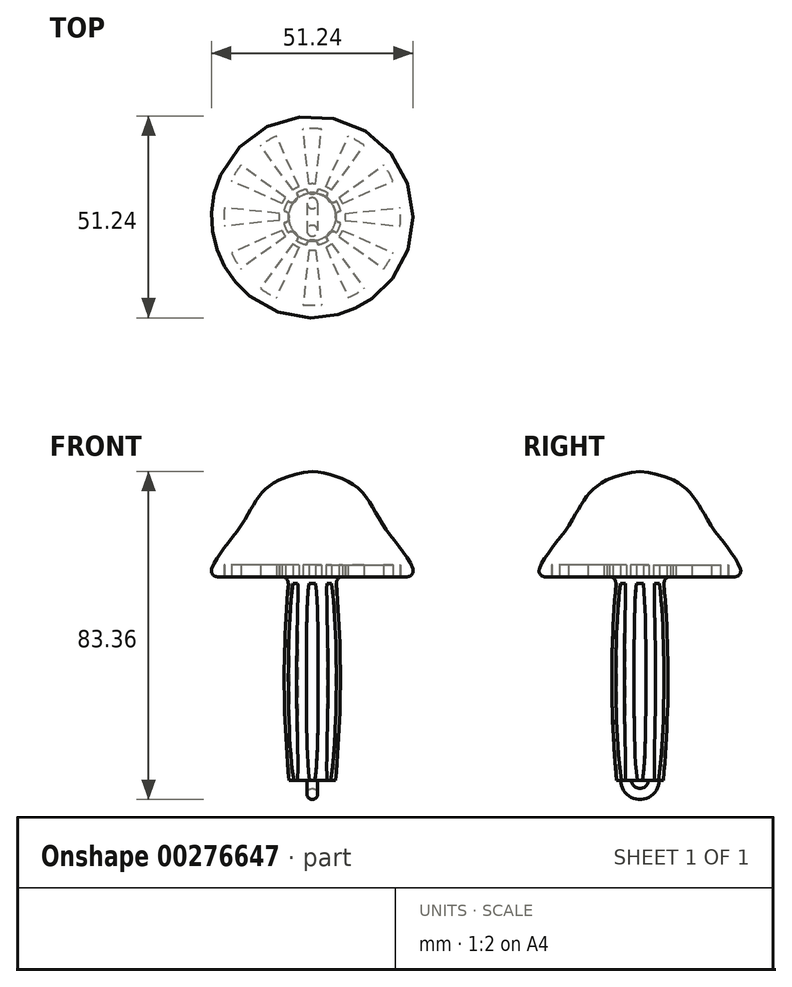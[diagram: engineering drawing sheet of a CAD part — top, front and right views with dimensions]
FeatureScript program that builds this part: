
annotation { "Feature Type Name" : "Feature", "Feature Type Description" : "" }
export const myFeature = defineFeature(function(context is Context, id is Id, definition is map)
    precondition{}
    {
        {
            var Q0;
            Q0=qCreatedBy(makeId("Front.planeOp"),FACE);
            var sketch = newSketch(context, id + "F0", { "sketchPlane" : qUnion([Q0])});
            skLineSegment(sketch, "E0", {"start": v(0, 0) * mm, "end": v(6, 0) * mm});
            skLineSegment(sketch, "E1", {"start": v(0, 69.05) * mm, "end": v(0, 0) * mm});
            skArc(sketch, "E2", {"start": v(6, 0) * mm, "mid": v(7.3, 25.84) * mm, "end": v(6, 51.68) * mm});
            skLineSegment(sketch, "E3", {"start": v(6, 51.68) * mm, "end": v(26, 51.68) * mm});
            skLineSegment(sketch, "E4", {"start": v(0, 69.05) * mm, "end": v(0, 78.48) * mm});
            skFitSpline(sketch, "E5", {"points": [v(26, 51.68) * mm, v(18.55, 63.96) * mm, v(11.44, 74.34) * mm, v(0, 78.48) * mm], "startDerivative": vector(-3.83, 37.04) * mm, "endDerivative": vector(-33.85, 3.07) * mm});
            skSolve(sketch);
        }
        {
            var Q0;
            Q0=makeQuery(id+"F0.imprint","IMPRINT",FACE,{"disambiguationData":[TD([[makeQuery(id+"F0.imprint","IMPRINT",EDGE,{"derivedFrom":sQuery(id+"F0.wireOp",EDGE,"E0")}),1.0]])]});
            var Q1;
            Q1=sQuery(id+"F0.wireOp",EDGE,"E1");
            revolve(context, id + "F1", {"entities" : qUnion([Q0]), "axis" : qUnion([Q1]), "revolveType" : RevolveType.FULL});
        }
        {
            var Q0;
            Q0=makeQuery(id+"F1.opRevolve","SWEPT_FACE",FACE,{"disambiguationData":[OSD([sQuery(id+"F0.wireOp",EDGE,"E3")])]});
            var Q1;
            Q1=makeQuery(id+"F1.opRevolve","SWEPT_FACE",FACE,{"disambiguationData":[OSD([sQuery(id+"F0.wireOp",EDGE,"Vve0fadS-4mgB-wVBS-b9aS-wJGoKtQ9clZr")])]});
            fillet(context, id + "F2", {"entities" : qUnion([Q0, Q1]), "radius" : 1.5 * mm, "tangentPropagation" : true, "allowEdgeOverflow" : false});
        }
        {
            var Q0;
            Q0=qCreatedBy(makeId("Top.planeOp"),FACE);
            var sketch = newSketch(context, id + "F3", { "sketchPlane" : qUnion([Q0])});
            skLineSegment(sketch, "E6", {"start": v(0, 0) * mm, "end": v(14.37, 0) * mm, "construction": true});
            skCircle(sketch, "E7", {"center": v(0, -3.5) * mm, "radius": 1.38 * mm});
            skSolve(sketch);
        }
        {
            var Q0;
            Q0 = qSketchRegion(id + "F3", true);
            var Q1;
            Q1=sQuery(id+"F3.wireOp",EDGE,"E6");
            revolve(context, id + "F4", {"operationType" : NewBodyOperationType.ADD, "entities" : qUnion([Q0]), "axis" : qUnion([Q1]), "revolveType" : RevolveType.ONE_DIRECTION, "angle" : 180 * degree});
        }
        {
            var Q0;
            Q0=makeQuery(id+"F1.opRevolve","SWEPT_FACE",FACE,{"disambiguationData":[OSD([sQuery(id+"F0.wireOp",EDGE,"E0")])]});
            var sketch = newSketch(context, id + "F5", { "sketchPlane" : qUnion([Q0])});
            skLineSegment(sketch, "E8", {"start": v(0, 0) * mm, "end": v(0, 7.31) * mm});
            skCircle(sketch, "E9", {"center": v(0, 7.31) * mm, "radius": 1.5 * mm});
            skCircle(sketch, "E10.1.0", {"center": v(-5.17, 5.17) * mm, "radius": 1.5 * mm});
            skCircle(sketch, "E10.2.0", {"center": v(-7.31, 0) * mm, "radius": 1.5 * mm});
            skCircle(sketch, "E10.3.0", {"center": v(-5.17, -5.17) * mm, "radius": 1.5 * mm});
            skCircle(sketch, "E10.4.0", {"center": v(0, -7.31) * mm, "radius": 1.5 * mm});
            skCircle(sketch, "E10.5.0", {"center": v(5.17, -5.17) * mm, "radius": 1.5 * mm});
            skCircle(sketch, "E10.6.0", {"center": v(7.31, 0) * mm, "radius": 1.5 * mm});
            skCircle(sketch, "E10.7.0", {"center": v(5.17, 5.17) * mm, "radius": 1.5 * mm});
            skPoint(sketch, "E10.center", {"position": v(0, 0) * mm});
            skSolve(sketch);
        }
        {
            var Q0;
            Q0 = qSketchRegion(id + "F5", true);
            extrude(context, id + "F6", {"entities" : qUnion([Q0]), "operationType" : NewBodyOperationType.REMOVE, "oppositeDirection" : true, "depth" : 50 * mm});
        }
        {
            var Q0;
            Q0=makeQuery(id+"F1.opRevolve","SWEPT_FACE",FACE,{"disambiguationData":[OSD([sQuery(id+"F0.wireOp",EDGE,"E3")])]});
            var sketch = newSketch(context, id + "F7", { "sketchPlane" : qUnion([Q0])});
            skLineSegment(sketch, "E11", {"start": v(0.88, 8.37) * mm, "end": v(2.35, 22.32) * mm});
            skLineSegment(sketch, "E12", {"start": v(-0.88, 8.37) * mm, "end": v(-2.35, 22.32) * mm});
            skArc(sketch, "E13", {"start": v(0.88, 8.37) * mm, "mid": v(0, 8.42) * mm, "end": v(-0.88, 8.37) * mm});
            skArc(sketch, "E14", {"start": v(2.35, 22.32) * mm, "mid": v(0, 22.44) * mm, "end": v(-2.35, 22.32) * mm});
            skPoint(sketch, "E15.trimOffspring.end.orphan", {"position": v(0, 28.12) * mm});
            skPoint(sketch, "E16.orphan", {"position": v(2.96, 28.12) * mm});
            skArc(sketch, "E17.1.0", {"start": v(-9.13, 20.5) * mm, "mid": v(-11.22, 19.43) * mm, "end": v(-13.19, 18.15) * mm});
            skLineSegment(sketch, "E17.1.1", {"start": v(-3.42, 7.7) * mm, "end": v(-9.13, 20.5) * mm});
            skLineSegment(sketch, "E17.1.2", {"start": v(-4.95, 6.81) * mm, "end": v(-13.19, 18.15) * mm});
            skArc(sketch, "E17.1.3", {"start": v(-3.42, 7.7) * mm, "mid": v(-4.2, 7.3) * mm, "end": v(-4.95, 6.81) * mm});
            skArc(sketch, "E17.2.0", {"start": v(-18.15, 13.19) * mm, "mid": v(-19.43, 11.22) * mm, "end": v(-20.5, 9.13) * mm});
            skLineSegment(sketch, "E17.2.1", {"start": v(-6.81, 4.95) * mm, "end": v(-18.15, 13.19) * mm});
            skLineSegment(sketch, "E17.2.2", {"start": v(-7.7, 3.42) * mm, "end": v(-20.5, 9.13) * mm});
            skArc(sketch, "E17.2.3", {"start": v(-6.81, 4.95) * mm, "mid": v(-7.3, 4.2) * mm, "end": v(-7.7, 3.42) * mm});
            skArc(sketch, "E17.3.0", {"start": v(-22.32, 2.35) * mm, "mid": v(-22.44, 0) * mm, "end": v(-22.32, -2.35) * mm});
            skLineSegment(sketch, "E17.3.1", {"start": v(-8.37, 0.88) * mm, "end": v(-22.32, 2.35) * mm});
            skLineSegment(sketch, "E17.3.2", {"start": v(-8.37, -0.88) * mm, "end": v(-22.32, -2.35) * mm});
            skArc(sketch, "E17.3.3", {"start": v(-8.37, 0.88) * mm, "mid": v(-8.42, 0) * mm, "end": v(-8.37, -0.88) * mm});
            skArc(sketch, "E17.4.0", {"start": v(-20.5, -9.13) * mm, "mid": v(-19.43, -11.22) * mm, "end": v(-18.15, -13.19) * mm});
            skLineSegment(sketch, "E17.4.1", {"start": v(-7.7, -3.42) * mm, "end": v(-20.5, -9.13) * mm});
            skLineSegment(sketch, "E17.4.2", {"start": v(-6.81, -4.95) * mm, "end": v(-18.15, -13.19) * mm});
            skArc(sketch, "E17.4.3", {"start": v(-7.7, -3.42) * mm, "mid": v(-7.3, -4.2) * mm, "end": v(-6.81, -4.95) * mm});
            skArc(sketch, "E17.5.0", {"start": v(-13.19, -18.15) * mm, "mid": v(-11.22, -19.43) * mm, "end": v(-9.13, -20.5) * mm});
            skLineSegment(sketch, "E17.5.1", {"start": v(-4.95, -6.81) * mm, "end": v(-13.19, -18.15) * mm});
            skLineSegment(sketch, "E17.5.2", {"start": v(-3.42, -7.7) * mm, "end": v(-9.13, -20.5) * mm});
            skArc(sketch, "E17.5.3", {"start": v(-4.95, -6.81) * mm, "mid": v(-4.2, -7.3) * mm, "end": v(-3.42, -7.7) * mm});
            skArc(sketch, "E17.6.0", {"start": v(-2.35, -22.32) * mm, "mid": v(0, -22.44) * mm, "end": v(2.35, -22.32) * mm});
            skLineSegment(sketch, "E17.6.1", {"start": v(-0.88, -8.37) * mm, "end": v(-2.35, -22.32) * mm});
            skLineSegment(sketch, "E17.6.2", {"start": v(0.88, -8.37) * mm, "end": v(2.35, -22.32) * mm});
            skArc(sketch, "E17.6.3", {"start": v(-0.88, -8.37) * mm, "mid": v(0, -8.42) * mm, "end": v(0.88, -8.37) * mm});
            skArc(sketch, "E17.7.0", {"start": v(9.13, -20.5) * mm, "mid": v(11.22, -19.43) * mm, "end": v(13.19, -18.15) * mm});
            skLineSegment(sketch, "E17.7.1", {"start": v(3.42, -7.7) * mm, "end": v(9.13, -20.5) * mm});
            skLineSegment(sketch, "E17.7.2", {"start": v(4.95, -6.81) * mm, "end": v(13.19, -18.15) * mm});
            skArc(sketch, "E17.7.3", {"start": v(3.42, -7.7) * mm, "mid": v(4.2, -7.3) * mm, "end": v(4.95, -6.81) * mm});
            skArc(sketch, "E17.8.0", {"start": v(18.15, -13.19) * mm, "mid": v(19.43, -11.22) * mm, "end": v(20.5, -9.13) * mm});
            skLineSegment(sketch, "E17.8.1", {"start": v(6.81, -4.95) * mm, "end": v(18.15, -13.19) * mm});
            skLineSegment(sketch, "E17.8.2", {"start": v(7.7, -3.42) * mm, "end": v(20.5, -9.13) * mm});
            skArc(sketch, "E17.8.3", {"start": v(6.81, -4.95) * mm, "mid": v(7.3, -4.2) * mm, "end": v(7.7, -3.42) * mm});
            skArc(sketch, "E17.9.0", {"start": v(22.32, -2.35) * mm, "mid": v(22.44, 0) * mm, "end": v(22.32, 2.35) * mm});
            skLineSegment(sketch, "E17.9.1", {"start": v(8.37, -0.88) * mm, "end": v(22.32, -2.35) * mm});
            skLineSegment(sketch, "E17.9.2", {"start": v(8.37, 0.88) * mm, "end": v(22.32, 2.35) * mm});
            skArc(sketch, "E17.9.3", {"start": v(8.37, -0.88) * mm, "mid": v(8.42, 0) * mm, "end": v(8.37, 0.88) * mm});
            skArc(sketch, "E17.10.0", {"start": v(20.5, 9.13) * mm, "mid": v(19.43, 11.22) * mm, "end": v(18.15, 13.19) * mm});
            skLineSegment(sketch, "E17.10.1", {"start": v(7.7, 3.42) * mm, "end": v(20.5, 9.13) * mm});
            skLineSegment(sketch, "E17.10.2", {"start": v(6.81, 4.95) * mm, "end": v(18.15, 13.19) * mm});
            skArc(sketch, "E17.10.3", {"start": v(7.7, 3.42) * mm, "mid": v(7.3, 4.2) * mm, "end": v(6.81, 4.95) * mm});
            skArc(sketch, "E17.11.0", {"start": v(13.19, 18.15) * mm, "mid": v(11.22, 19.43) * mm, "end": v(9.13, 20.5) * mm});
            skLineSegment(sketch, "E17.11.1", {"start": v(4.95, 6.81) * mm, "end": v(13.19, 18.15) * mm});
            skLineSegment(sketch, "E17.11.2", {"start": v(3.42, 7.7) * mm, "end": v(9.13, 20.5) * mm});
            skArc(sketch, "E17.11.3", {"start": v(4.95, 6.81) * mm, "mid": v(4.2, 7.3) * mm, "end": v(3.42, 7.7) * mm});
            skSolve(sketch);
        }
        {
            var Q0;
            Q0 = qSketchRegion(id + "F7", true);
            extrude(context, id + "F8", {"entities" : qUnion([Q0]), "operationType" : NewBodyOperationType.REMOVE, "oppositeDirection" : true, "depth" : 3 * mm});
        }
    });
